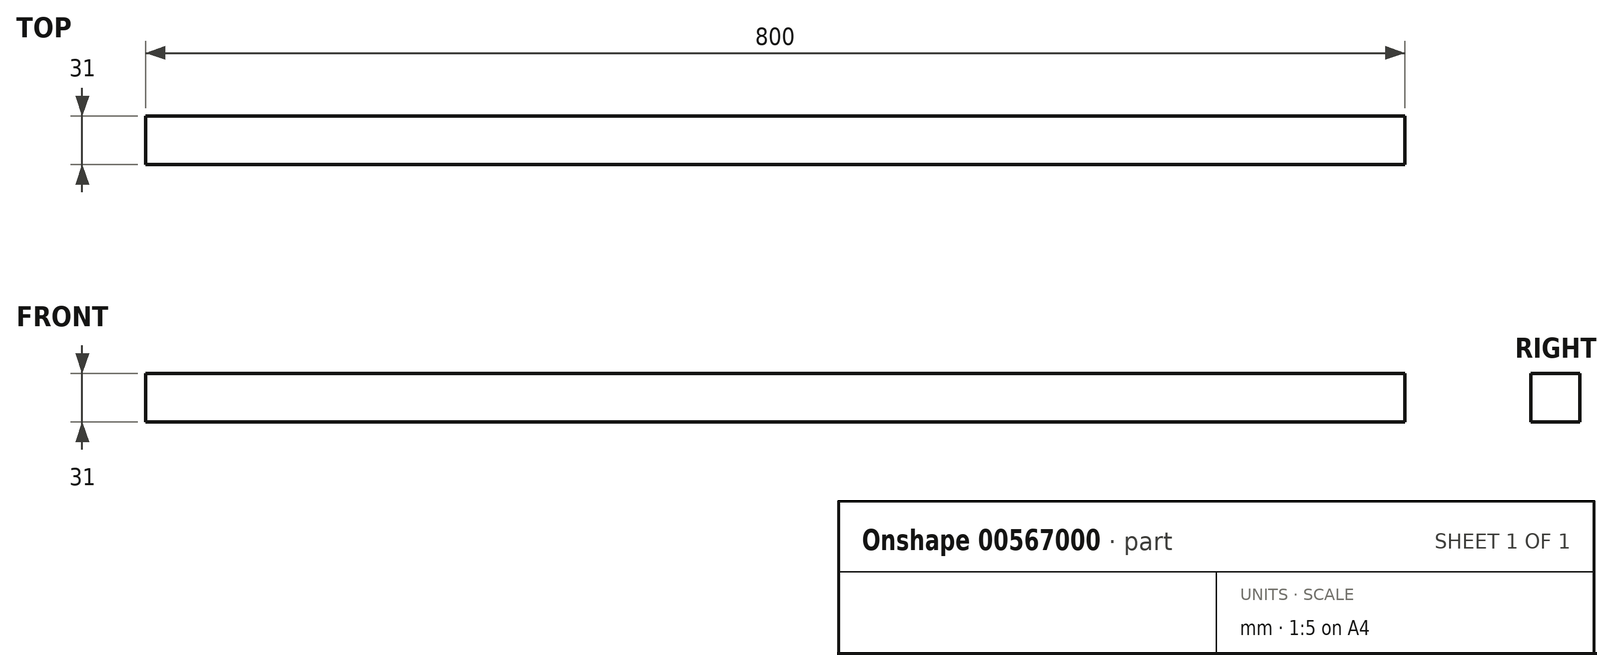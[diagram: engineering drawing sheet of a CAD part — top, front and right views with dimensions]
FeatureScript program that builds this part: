
annotation { "Feature Type Name" : "Feature", "Feature Type Description" : "" }
export const myFeature = defineFeature(function(context is Context, id is Id, definition is map)
    precondition{}
    {
        {
            var Q0;
            Q0=qCreatedBy(makeId("Front.planeOp"),FACE);
            var sketch = newSketch(context, id + "F0", { "sketchPlane" : qUnion([Q0])});
            skLineSegment(sketch, "E0.bottom", {"start": v(-47.64, 65.23) * mm, "end": v(752.36, 65.23) * mm});
            skLineSegment(sketch, "E0.top", {"start": v(-47.64, 34.23) * mm, "end": v(752.36, 34.23) * mm});
            skLineSegment(sketch, "E0.left", {"start": v(-47.64, 65.23) * mm, "end": v(-47.64, 34.23) * mm});
            skLineSegment(sketch, "E0.right", {"start": v(752.36, 65.23) * mm, "end": v(752.36, 34.23) * mm});
            skSolve(sketch);
        }
        {
            var Q0;
            Q0 = qSketchRegion(id + "F0", true);
            extrude(context, id + "F1", {"entities" : qUnion([Q0]), "depth" : 31 * mm, "offsetDistance" : 25 * mm});
        }
    });
